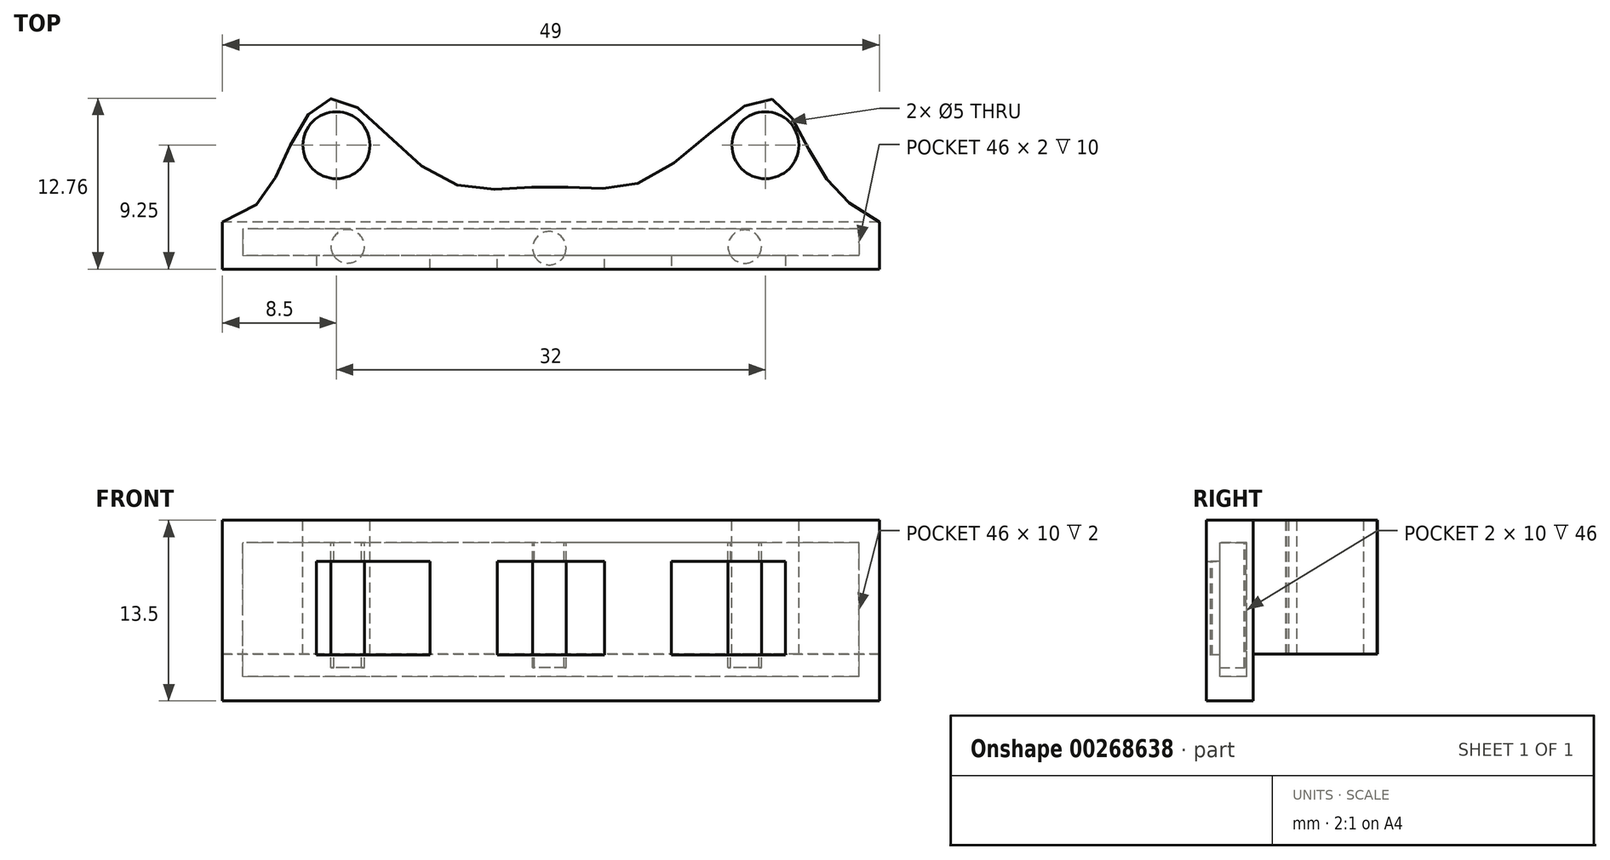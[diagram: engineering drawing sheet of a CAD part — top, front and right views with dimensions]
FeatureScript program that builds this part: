
annotation { "Feature Type Name" : "Feature", "Feature Type Description" : "" }
export const myFeature = defineFeature(function(context is Context, id is Id, definition is map)
    precondition{}
    {
        {
            var Q0;
            Q0=qCreatedBy(makeId("Top.planeOp"),FACE);
            var sketch = newSketch(context, id + "F0", { "sketchPlane" : qUnion([Q0])});
            skLineSegment(sketch, "E0.bottom", {"start": v(24.5, -1.25) * mm, "end": v(-24.5, -1.25) * mm});
            skLineSegment(sketch, "E0.top", {"start": v(24.5, 1.25) * mm, "end": v(-24.5, 1.25) * mm});
            skLineSegment(sketch, "E0.left", {"start": v(24.5, -1.25) * mm, "end": v(24.5, 1.25) * mm});
            skLineSegment(sketch, "E0.right", {"start": v(-24.5, -1.25) * mm, "end": v(-24.5, 1.25) * mm});
            skPoint(sketch, "E0.middle", {"position": v(0, 0) * mm});
            skFitSpline(sketch, "E1", {"points": [v(-24.5, 1.25) * mm, v(-19.68, 6.51) * mm, v(-15.96, 10.5) * mm, v(-8.4, 4.6) * mm, v(0, 3.92) * mm, v(7.53, 4.6) * mm, v(16.09, 10.5) * mm, v(19.56, 6.1) * mm, v(24.5, 1.25) * mm], "startDerivative": vector(76.87, 19.5) * mm, "endDerivative": vector(59.53, -29.95) * mm});
            skPoint(sketch, "E2", {"position": v(-16, 7) * mm});
            skPoint(sketch, "E3", {"position": v(16, 7) * mm});
            skSolve(sketch);
        }
        {
            var Q0;
            Q0=makeQuery(id+"F0.imprint","IMPRINT",FACE,{"disambiguationData":[TD([[makeQuery(id+"F0.imprint","IMPRINT",EDGE,{"derivedFrom":sQuery(id+"F0.wireOp",EDGE,"E0.bottom")}),-1.0]])]});
            extrude(context, id + "F1", {"entities" : qUnion([Q0]), "oppositeDirection" : true, "depth" : 11.5 * mm, "offsetDistance" : 25 * mm});
        }
        {
            var Q0;
            Q0=makeQuery(id+"F0.imprint","IMPRINT",FACE,{"disambiguationData":[TD([[makeQuery(id+"F0.imprint","IMPRINT",EDGE,{"derivedFrom":sQuery(id+"F0.wireOp",EDGE,"E0.top")}),-1.0]])]});
            extrude(context, id + "F2", {"entities" : qUnion([Q0]), "operationType" : NewBodyOperationType.ADD, "oppositeDirection" : true, "depth" : 9 * mm});
        }
        {
            var Q0;
            Q0=sQuery(id+"F0.wireOp",VERTEX,"E2");
            var Q1;
            Q1=sQuery(id+"F0.wireOp",VERTEX,"E3");
            var Q2;
            Q2=makeQuery(id+"F1.opExtrude","SWEPT_BODY",BODY,{"disambiguationData":[OSD([sQuery(id+"F0.wireOp",EDGE,"E0.bottom"),sQuery(id+"F0.wireOp",EDGE,"E0.top"),sQuery(id+"F0.wireOp",EDGE,"E0.left"),sQuery(id+"F0.wireOp",EDGE,"E0.right"),sQuery(id+"F0.wireOp",EDGE,"qSG4pFbB-mWNJ-fMbz-A37t-o3lnEbjPYmPd.bottom"),sQuery(id+"F0.wireOp",EDGE,"qSG4pFbB-mWNJ-fMbz-A37t-o3lnEbjPYmPd.top"),sQuery(id+"F0.wireOp",EDGE,"qSG4pFbB-mWNJ-fMbz-A37t-o3lnEbjPYmPd.left"),sQuery(id+"F0.wireOp",EDGE,"qSG4pFbB-mWNJ-fMbz-A37t-o3lnEbjPYmPd.right")])]});
            hole(context, id + "F3", {"style" : HoleStyle.SIMPLE, "endStyle" : HoleEndStyle.THROUGH, "holeDiameter" : 5 * mm, "tappedDepth" : 12 * mm, "tapClearance" : 3, "locations" : qUnion([Q0, Q1]), "scope" : qUnion([Q2])});
        }
        {
            var Q0;
            Q0=makeQuery(id+"F1.opExtrude","SWEPT_FACE",FACE,{"disambiguationData":[OSD([sQuery(id+"F0.wireOp",EDGE,"E0.bottom")])]});
            var sketch = newSketch(context, id + "F4", { "sketchPlane" : qUnion([Q0])});
            skLineSegment(sketch, "E4.bottom", {"start": v(23, -10.69) * mm, "end": v(-23, -10.69) * mm});
            skLineSegment(sketch, "E4.top", {"start": v(23, -0.69) * mm, "end": v(-23, -0.69) * mm});
            skLineSegment(sketch, "E4.left", {"start": v(23, -10.69) * mm, "end": v(23, -0.69) * mm});
            skLineSegment(sketch, "E4.right", {"start": v(-23, -10.69) * mm, "end": v(-23, -0.69) * mm});
            skPoint(sketch, "E4.middle", {"position": v(0, -5.69) * mm});
            skSolve(sketch);
        }
        {
            var Q0;
            Q0=makeQuery(id+"F4.imprint","IMPRINT",FACE,{"disambiguationData":[TD([[makeQuery(id+"F4.imprint","IMPRINT",EDGE,{"derivedFrom":sQuery(id+"F4.wireOp",EDGE,"E4.bottom")}),-1.0]])]});
            extrude(context, id + "F5", {"entities" : qUnion([Q0]), "operationType" : NewBodyOperationType.REMOVE, "oppositeDirection" : true, "depth" : 2 * mm});
        }
        {
            var Q0;
            Q0=makeQuery(id+"F1.opExtrude","SWEPT_FACE",FACE,{"disambiguationData":[OSD([sQuery(id+"F0.wireOp",EDGE,"E0.bottom")])]});
            var sketch = newSketch(context, id + "F6", { "sketchPlane" : qUnion([Q0])});
            skLineSegment(sketch, "E5.bottom", {"start": v(-24.5, 0) * mm, "end": v(24.5, 0) * mm});
            skLineSegment(sketch, "E5.top", {"start": v(-24.5, -11.5) * mm, "end": v(24.5, -11.5) * mm});
            skLineSegment(sketch, "E5.left", {"start": v(-24.5, 0) * mm, "end": v(-24.5, -11.5) * mm});
            skLineSegment(sketch, "E5.right", {"start": v(24.5, 0) * mm, "end": v(24.5, -11.5) * mm});
            skSolve(sketch);
        }
        {
            var Q0;
            Q0=qSketchRegion(id+"F6",true);
            extrude(context, id + "F7", {"entities" : qUnion([Q0]), "operationType" : NewBodyOperationType.ADD, "depth" : 1 * mm});
        }
        {
            var Q0;
            Q0=makeQuery(id+"F7.opExtrude","CAP_FACE",FACE,{"disambiguationData":[OSD([sQuery(id+"F6.wireOp",EDGE,"E5.bottom"),sQuery(id+"F6.wireOp",EDGE,"E5.top"),sQuery(id+"F6.wireOp",EDGE,"E5.left"),sQuery(id+"F6.wireOp",EDGE,"E5.right")])],"isStart":false});
            var sketch = newSketch(context, id + "F8", { "sketchPlane" : qUnion([Q0])});
            skLineSegment(sketch, "E6.bottom", {"start": v(17.5, -9.07) * mm, "end": v(-17.5, -9.07) * mm});
            skLineSegment(sketch, "E6.top", {"start": v(17.5, -2.07) * mm, "end": v(-17.5, -2.07) * mm});
            skLineSegment(sketch, "E6.left", {"start": v(17.5, -9.07) * mm, "end": v(17.5, -2.07) * mm});
            skLineSegment(sketch, "E6.right", {"start": v(-17.5, -9.07) * mm, "end": v(-17.5, -2.07) * mm});
            skPoint(sketch, "E6.middle", {"position": v(0, -5.57) * mm});
            skSolve(sketch);
        }
        {
            var Q0;
            Q0=makeQuery(id+"F8.imprint","IMPRINT",FACE,{"disambiguationData":[TD([[makeQuery(id+"F8.imprint","IMPRINT",EDGE,{"derivedFrom":sQuery(id+"F8.wireOp",EDGE,"E6.bottom")}),-1.0]])]});
            extrude(context, id + "F9", {"entities" : qUnion([Q0]), "operationType" : NewBodyOperationType.REMOVE, "oppositeDirection" : true, "depth" : 2 * mm});
        }
        {
            var Q0;
            {var subQ0=sQuery(id+"F0.wireOp",EDGE,"E0.top");Q0=makeQuery(id+"F7.boolean.opBoolean","MERGE",FACE,{"derivedFrom":[makeQuery(id+"F2.boolean.opBoolean","MERGE",FACE,{"derivedFrom":[makeQuery(id+"F1.opExtrude","CAP_FACE",FACE,{"disambiguationData":[OSD([sQuery(id+"F0.wireOp",EDGE,"E0.bottom"),subQ0,sQuery(id+"F0.wireOp",EDGE,"E0.left"),sQuery(id+"F0.wireOp",EDGE,"E0.right")])],"isStart":true}),makeQuery(id+"F2.opExtrude","CAP_FACE",FACE,{"disambiguationData":[OSD([subQ0,sQuery(id+"F0.wireOp",EDGE,"E1")])],"isStart":true})]}),makeQuery(id+"F7.opExtrude","SWEPT_FACE",FACE,{"disambiguationData":[OSD([sQuery(id+"F6.wireOp",EDGE,"E5.bottom")])]})]});}
            var sketch = newSketch(context, id + "F10", { "sketchPlane" : qUnion([Q0])});
            skCircle(sketch, "E7", {"center": v(-15.16, -0.55) * mm, "radius": 1.25 * mm});
            skCircle(sketch, "E8", {"center": v(14.46, -0.57) * mm, "radius": 1.25 * mm});
            skCircle(sketch, "E9", {"center": v(-0.11, -0.69) * mm, "radius": 1.25 * mm});
            skSolve(sketch);
        }
        {
            var Q0;
            Q0=makeQuery(id+"F10.imprint","IMPRINT",FACE,{"disambiguationData":[TD([[makeQuery(id+"F10.imprint","IMPRINT",EDGE,{"derivedFrom":sQuery(id+"F10.wireOp",EDGE,"E7")}),1.0]])]});
            var Q1;
            Q1=makeQuery(id+"F10.imprint","IMPRINT",FACE,{"disambiguationData":[TD([[makeQuery(id+"F10.imprint","IMPRINT",EDGE,{"derivedFrom":sQuery(id+"F10.wireOp",EDGE,"0a53f06c-6a5f-48a1-aa67-1fc5956b9cec")}),1.0]])]});
            var Q2;
            Q2=makeQuery(id+"F10.imprint","IMPRINT",FACE,{"disambiguationData":[TD([[makeQuery(id+"F10.imprint","IMPRINT",EDGE,{"derivedFrom":sQuery(id+"F10.wireOp",EDGE,"E9")}),1.0]])]});
            var Q3;
            Q3=makeQuery(id+"F10.imprint","IMPRINT",FACE,{"disambiguationData":[TD([[makeQuery(id+"F10.imprint","IMPRINT",EDGE,{"derivedFrom":sQuery(id+"F10.wireOp",EDGE,"b2b61686-fe17-4c86-8418-5b016842f24e")}),1.0]])]});
            var Q4;
            Q4=makeQuery(id+"F10.imprint","IMPRINT",FACE,{"disambiguationData":[TD([[makeQuery(id+"F10.imprint","IMPRINT",EDGE,{"derivedFrom":sQuery(id+"F10.wireOp",EDGE,"E8")}),1.0]])]});
            extrude(context, id + "F11", {"entities" : qUnion([Q0, Q1, Q2, Q3, Q4]), "operationType" : NewBodyOperationType.ADD, "oppositeDirection" : true, "depth" : 10 * mm, "offsetDistance" : 25 * mm});
        }
        {
            var Q0;
            Q0=makeQuery(id+"F7.boolean.opBoolean","MERGE",FACE,{"derivedFrom":[makeQuery(id+"F1.opExtrude","CAP_FACE",FACE,{"disambiguationData":[OSD([sQuery(id+"F0.wireOp",EDGE,"E0.bottom"),sQuery(id+"F0.wireOp",EDGE,"E0.top"),sQuery(id+"F0.wireOp",EDGE,"E0.left"),sQuery(id+"F0.wireOp",EDGE,"E0.right")])],"isStart":false}),makeQuery(id+"F7.opExtrude","SWEPT_FACE",FACE,{"disambiguationData":[OSD([sQuery(id+"F6.wireOp",EDGE,"E5.top")])]})]});
            extrude(context, id + "F12", {"entities" : qUnion([Q0]), "operationType" : NewBodyOperationType.ADD, "depth" : 1 * mm, "offsetDistance" : 25 * mm});
        }
        {
            var Q0;
            Q0=makeQuery(id+"F10.imprint","IMPRINT",FACE,{"disambiguationData":[TD([[makeQuery(id+"F10.imprint","IMPRINT",EDGE,{"derivedFrom":sQuery(id+"F10.wireOp",EDGE,"E7")}),-1.0]])]});
            extrude(context, id + "F13", {"entities" : qUnion([Q0]), "operationType" : NewBodyOperationType.ADD, "depth" : 1 * mm, "offsetDistance" : 25 * mm});
        }
        {
            var Q0;
            Q0=makeQuery(id+"F10.imprint","IMPRINT",FACE,{"disambiguationData":[TD([[makeQuery(id+"F10.imprint","IMPRINT",EDGE,{"derivedFrom":sQuery(id+"F10.wireOp",EDGE,"E7")}),1.0]])]});
            var Q1;
            Q1=makeQuery(id+"F10.imprint","IMPRINT",FACE,{"disambiguationData":[TD([[makeQuery(id+"F10.imprint","IMPRINT",EDGE,{"derivedFrom":sQuery(id+"F10.wireOp",EDGE,"0a53f06c-6a5f-48a1-aa67-1fc5956b9cec")}),1.0]])]});
            var Q2;
            Q2=makeQuery(id+"F10.imprint","IMPRINT",FACE,{"disambiguationData":[TD([[makeQuery(id+"F10.imprint","IMPRINT",EDGE,{"derivedFrom":sQuery(id+"F10.wireOp",EDGE,"b2b61686-fe17-4c86-8418-5b016842f24e")}),1.0]])]});
            var Q3;
            Q3=makeQuery(id+"F10.imprint","IMPRINT",FACE,{"disambiguationData":[TD([[makeQuery(id+"F10.imprint","IMPRINT",EDGE,{"derivedFrom":sQuery(id+"F10.wireOp",EDGE,"E9")}),1.0]])]});
            var Q4;
            Q4=makeQuery(id+"F10.imprint","IMPRINT",FACE,{"disambiguationData":[TD([[makeQuery(id+"F10.imprint","IMPRINT",EDGE,{"derivedFrom":sQuery(id+"F10.wireOp",EDGE,"E8")}),1.0]])]});
            extrude(context, id + "F14", {"entities" : qUnion([Q0, Q1, Q2, Q3, Q4]), "operationType" : NewBodyOperationType.ADD, "depth" : 1 * mm, "offsetDistance" : 25 * mm});
        }
        {
            var Q0;
            Q0=makeQuery(id+"F9.boolean.opBoolean","COPY",FACE,{"derivedFrom":makeQuery(id+"F9.opExtrude","SWEPT_FACE",FACE,{"disambiguationData":[OSD([sQuery(id+"F8.wireOp",EDGE,"E6.bottom")])]})});
            var sketch = newSketch(context, id + "F15", { "sketchPlane" : qUnion([Q0])});
            skLineSegment(sketch, "E10.bottom", {"start": v(-9, -1.25) * mm, "end": v(-4, -1.25) * mm});
            skLineSegment(sketch, "E10.top", {"start": v(-9, -2.25) * mm, "end": v(-4, -2.25) * mm});
            skLineSegment(sketch, "E10.left", {"start": v(-9, -1.25) * mm, "end": v(-9, -2.25) * mm});
            skLineSegment(sketch, "E10.right", {"start": v(-4, -1.25) * mm, "end": v(-4, -2.25) * mm});
            skLineSegment(sketch, "E11.bottom", {"start": v(4, -1.25) * mm, "end": v(9, -1.25) * mm});
            skLineSegment(sketch, "E11.top", {"start": v(4, -2.25) * mm, "end": v(9, -2.25) * mm});
            skLineSegment(sketch, "E11.left", {"start": v(4, -1.25) * mm, "end": v(4, -2.25) * mm});
            skLineSegment(sketch, "E11.right", {"start": v(9, -1.25) * mm, "end": v(9, -2.25) * mm});
            skSolve(sketch);
        }
        {
            var Q0;
            Q0=makeQuery(id+"F15.imprint","IMPRINT",FACE,{"disambiguationData":[TD([[makeQuery(id+"F15.imprint","IMPRINT",EDGE,{"derivedFrom":sQuery(id+"F15.wireOp",EDGE,"E10.bottom")}),1.0]])]});
            var Q1;
            Q1=makeQuery(id+"F15.imprint","IMPRINT",FACE,{"disambiguationData":[TD([[makeQuery(id+"F15.imprint","IMPRINT",EDGE,{"derivedFrom":sQuery(id+"F15.wireOp",EDGE,"E11.bottom")}),1.0]])]});
            extrude(context, id + "F16", {"entities" : qUnion([Q0, Q1]), "operationType" : NewBodyOperationType.ADD, "depth" : 8 * mm, "offsetDistance" : 25 * mm});
        }
    });
